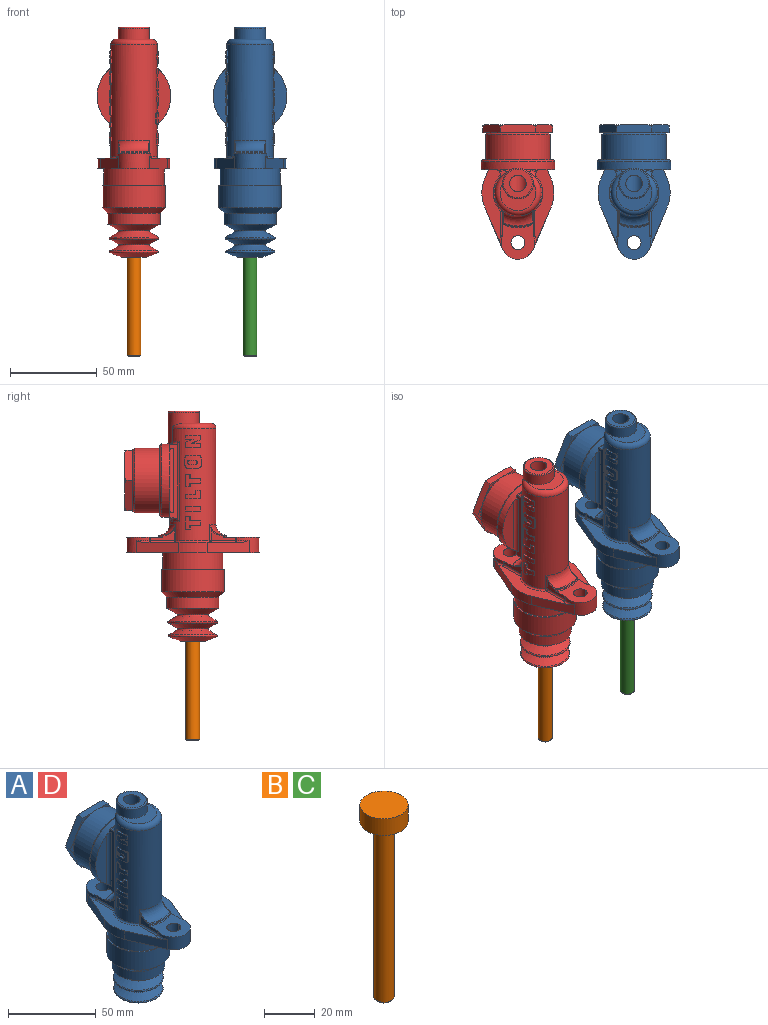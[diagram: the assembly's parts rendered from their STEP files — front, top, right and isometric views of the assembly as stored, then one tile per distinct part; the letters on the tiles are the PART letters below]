
ASSEMBLY  parts=4 mates=7
PART A: 264 faces, bbox 46.8x78.4x133.3 mm
  f0: torus R=9.44mm, axis (0,0,1), area 75.5mm2, adj f28,f29
  f1: torus R=9.44mm, axis (0,0,1), area 75.5mm2, adj f31,f32
  f2: cylinder r=14.05mm len=8.75mm, axis (0,0,1), area 34.9mm2, adj f197,f198,f199,f200,f201,f202,f203,f204
  f3: cylinder r=14.05mm len=8.75mm, axis (0,0,1), area 34.9mm2, adj f189,f190,f191,f192,f193,f194,f195,f196
  f4: cylinder r=13.3mm len=5.19mm, axis (0,0,1), area 11.7mm2, adj f181,f182,f183,f184,f185,f186,f187,f188
  f5: cylinder r=14.05mm len=9.25mm, axis (0,0,1), area 54.7mm2, adj f173,f174,f175,f176,f177,f178,f179,f180
  f6: cylinder r=14.05mm len=8.75mm, axis (0,0,1), area 52.7mm2, adj f163,f164,f165,f166,f167,f168,f169,f170
  f7: cylinder r=14.05mm len=8.75mm, axis (0,0,1), area 29.3mm2, adj f157,f158,f159,f160,f161,f162
  f8: cylinder r=14.05mm len=8.75mm, axis (0,0,1), area 23.2mm2, adj f153,f154,f155,f156
  f9: torus R=10.54mm, axis (0,0,1), area 8.4mm2, adj f15,f46,f121,f140
  f10: torus R=14.3mm, axis (0,0,1), area 35.1mm2, adj f23,f121,f136,f138
  f11: torus R=10.54mm, axis (0,0,1), area 8.4mm2, adj f16,f44,f121,f133
  f12: cylinder r=4.76mm len=37.03mm, axis (0,0,1), area 1064.2mm2, adj f13,f78
  f13: cylinder r=5.56mm len=39mm, axis (0,1,0), area 1280.3mm2, adj f12,f14,f93
  f14: cone r=5.56mm half-angle=59deg, axis (0,1,0), area 113.1mm2, adj f13
  f15: cylinder r=9.54mm len=19.09mm, axis (0,0,-1), area 230mm2, adj f9,f41,f46,f48,f69,f114,f118,f122
  f16: cylinder r=9.54mm len=19.09mm, axis (0,0,-1), area 230mm2, adj f11,f44,f47,f69,f70,f113,f119,f132
  f17: cylinder r=4mm len=9mm, axis (0,0,-1), area 226.2mm2, adj f69,f70
  f18: torus R=8.25mm, axis (0,0,1), area 55.6mm2, adj f19,f78
  f19: cylinder r=8.9mm len=18.85mm, axis (0,0,1), area 522.9mm2, adj f18,f21,f22,f23,f36,f55,f58,f76
  f20: cylinder r=9.53mm len=35.94mm, axis (0,0,1), area 2150.9mm2, adj f71,f77
  f21: torus R=10.3mm, axis (0,0,1), area 275.9mm2, adj f19,f22,f23,f76
  f22: cylinder r=13.3mm len=7.53mm, axis (0,0,1), area 46.4mm2, adj f19,f21,f23,f105,f106
  f23: cylinder r=13.3mm len=64.53mm, axis (0,0,1), area 3284.5mm2, adj f10,f19,f21,f22,f43,f75,f100,f101
  f24: cylinder r=17.3mm len=34.6mm, axis (0,0,1), area 1054.4mm2, adj f69,f73
  f25: cylinder r=18mm len=36mm, axis (0,0,1), area 1440.3mm2, adj f26,f73
  f26: cone r=18mm half-angle=45deg, axis (0,0,1), area 439.8mm2, adj f25,f27
  f27: cylinder r=15mm len=30mm, axis (0,0,1), area 602.3mm2, adj f26,f28
  f28: cone r=15mm half-angle=60deg, axis (0,0,1), area 514.8mm2, adj f0,f27
  f29: cone r=9.11mm half-angle=59deg, axis (0,0,-1), area 420.1mm2, adj f0,f30
  f30: torus R=13.72mm, axis (0,0,1), area 120.9mm2, adj f29,f31
  f31: cone r=14.04mm half-angle=60deg, axis (0,0,1), area 414.1mm2, adj f1,f30
  f32: cone r=9.11mm half-angle=59deg, axis (0,0,-1), area 397.4mm2, adj f1,f33
  f33: torus R=13.5mm, axis (0,0,1), area 128.9mm2, adj f32,f34
  f34: cone r=13.72mm half-angle=70deg, axis (0,0,1), area 458mm2, adj f33,f72
  f35: cylinder r=3.97mm len=28.5mm, axis (0,0,1), area 710.7mm2, adj f71,f72
  f36: cone r=21.11mm half-angle=0.7deg, axis (0,-1,0), area 609.8mm2, adj f19,f39,f55,f58,f59,f61,f62,f63
  f37: cone r=18.65mm half-angle=40deg, axis (0,-1,0), area 155.9mm2, adj f38,f49,f50,f51,f52,f53,f54,f81
  f38: cylinder r=18.65mm len=37.3mm, axis (0,-1,0), area 1686.5mm2, adj f37,f60
  f39: torus R=19.42mm, axis (0,-1,0), area 294.3mm2, adj f36,f60
  f40: cylinder r=20.75mm len=16.29mm, axis (0,0,-1), area 100.4mm2, adj f47,f48,f69,f116
  f41: plane 20.13x19.09mm, normal (0,0,1), area 258.8mm2, adj f15,f79,f80,f114,f115,f117,f118,f151
  f42: cylinder r=19.5mm len=17.55mm, axis (0,0,1), area 4mm2, adj f112,f120,f142,f143,f144,f152
  f43: torus R=19.54mm, axis (0,0,1), area 168.9mm2, adj f23,f141,f142,f143,f144,f145
  f44: plane 24.38x10.53mm, normal (0.92,0.39,0), area 159.4mm2, adj f11,f16,f45,f69,f121
  f45: cylinder r=20.75mm len=16.29mm, axis (0,0,-1), area 100.4mm2, adj f44,f46,f69,f121
  f46: plane 24.37x10.52mm, normal (0.92,-0.39,0), area 159.3mm2, adj f9,f15,f45,f69,f121
  f47: plane 24.4x10.54mm, normal (-0.92,0.39,0), area 159.3mm2, adj f16,f40,f69,f116,f132
  f48: plane 24.41x10.56mm, normal (-0.92,-0.39,0), area 159.3mm2, adj f15,f40,f69,f116,f122
  f49: plane 10.15x5.86mm, normal (0,-1,0), area 12mm2, adj f37,f87,f88
  f50: plane 11.72x3.38mm, normal (0,-1,0), area 12mm2, adj f37,f88,f89
  f51: plane 10.15x5.86mm, normal (0,-1,0), area 12mm2, adj f37,f89,f90
  f52: plane 10.15x5.86mm, normal (0,-1,0), area 12mm2, adj f37,f90,f91
  f53: plane 11.72x3.38mm, normal (0,-1,0), area 12mm2, adj f37,f91,f92
  f54: plane 10.15x5.86mm, normal (0,-1,0), area 12mm2, adj f37,f87,f92
  f55: plane 1.85x0.44mm, normal (0,-1,0), area 0.4mm2, adj f19,f36,f105
  f56: plane 2.74x1.99mm, normal (0,0,-1), area 2.5mm2, adj f64,f65,f109
  f57: plane 2.74x1.99mm, normal (0,0,1), area 2.5mm2, adj f63,f66,f101
  f58: plane 1.85x0.44mm, normal (0,-1,0), area 0.4mm2, adj f19,f36,f100
  f59: plane 34.46x8.87mm, normal (0,-1,0), area 214.2mm2, adj f36,f110
  f60: plane 38.84x38.84mm, normal (0,1,0), area 92mm2, adj f38,f39
  f61: plane 34.46x8.87mm, normal (0,-1,0), area 214.2mm2, adj f36,f111
  f62: plane 4.58x1.9mm, normal (0,1,0), area 3.8mm2, adj f36,f65,f68,f105
  f63: plane 4.58x1.9mm, normal (0,1,0), area 3.8mm2, adj f36,f57,f66,f100
  f64: plane 21.61x4.14mm, normal (0,1,0), area 27.2mm2, adj f36,f56,f65,f66,f67,f104,f108
  f65: plane 43.54x4.25mm, normal (1,0,0), area 103.4mm2, adj f36,f56,f62,f64,f68,f106,f107,f109
  f66: plane 43.54x4.25mm, normal (-1,0,0), area 103.4mm2, adj f36,f57,f63,f64,f67,f101,f102,f103
  f67: plane 2.74x1.99mm, normal (0,0,-1), area 2.5mm2, adj f64,f66,f103
  f68: plane 2.74x1.99mm, normal (0,0,1), area 2.5mm2, adj f62,f65,f106
  f69: plane 76.2x41.5mm, normal (0,0,-1), area 1110.8mm2, adj f15,f16,f17,f24,f40,f44,f45,f46
  f70: plane 20.13x19.09mm, normal (0,0,1), area 258.5mm2, adj f16,f17,f112,f113,f119,f120,f152
  f71: plane 19.05x19.05mm, normal (0,0,1), area 235.5mm2, adj f20,f35
  f72: plane 14.31x14.31mm, normal (0,0,-1), area 111.4mm2, adj f34,f35
  f73: plane 36x36mm, normal (0,0,1), area 77.6mm2, adj f24,f25
  f74: cylinder r=19.5mm len=17.55mm, axis (0,0,1), area 4mm2, adj f115,f117,f148,f149,f150,f151
  f75: torus R=19.54mm, axis (0,0,1), area 168.9mm2, adj f23,f146,f147,f148,f149,f150
  f76: plane 20.6x15.49mm, normal (0,0,1), area 146.4mm2, adj f19,f21
  f77: plane 19.05x19.05mm, normal (0,0,-1), area 285mm2, adj f20
  f78: plane 16.5x16.5mm, normal (0,0,1), area 142.6mm2, adj f12,f18
  f79: cylinder r=4mm len=9mm, axis (0,0,-1), area 112.8mm2, adj f41,f69,f80
  f80: cylinder r=4mm len=9mm, axis (0,0,-1), area 112.8mm2, adj f41,f69,f79
  f81: plane 5.75x3.32mm, normal (0,1,0), area 1.4mm2, adj f37,f88
  f82: plane 5.75x3.32mm, normal (0,1,0), area 1.4mm2, adj f37,f89
  f83: plane 6.64x0.31mm, normal (0,1,0), area 1.4mm2, adj f37,f90
  f84: plane 5.75x3.32mm, normal (0,1,0), area 1.4mm2, adj f37,f91
  f85: plane 5.75x3.32mm, normal (0,1,0), area 1.4mm2, adj f37,f92
  f86: plane 6.64x0.31mm, normal (0,1,0), area 1.4mm2, adj f37,f87
  f87: plane 20.34x4.67mm, normal (0,0,1), area 89.8mm2, adj f49,f54,f86,f88,f92,f93,f95,f99
  f88: plane 17.64x10.25mm, normal (-0.87,0,0.5), area 89.8mm2, adj f49,f50,f81,f87,f89,f93,f98,f99
  f89: plane 17.64x10.25mm, normal (-0.87,0,-0.5), area 89.8mm2, adj f50,f51,f82,f88,f90,f93,f97,f98
  f90: plane 20.34x4.67mm, normal (0,0,-1), area 89.8mm2, adj f51,f52,f83,f89,f91,f93,f96,f97
  f91: plane 17.64x10.25mm, normal (0.87,0,-0.5), area 89.8mm2, adj f52,f53,f84,f90,f92,f93,f94,f96
  f92: plane 17.64x10.25mm, normal (0.87,0,0.5), area 89.8mm2, adj f53,f54,f85,f87,f91,f93,f94,f95
  f93: plane 38.33x34.93mm, normal (0,1,0), area 948.4mm2, adj f13,f87,f88,f89,f90,f91,f92,f94
  f94: torus R=17.89mm, axis (0,-1,0), area 2.2mm2, adj f91,f92,f93
  f95: torus R=17.89mm, axis (0,-1,0), area 2.2mm2, adj f87,f92,f93
  f96: torus R=17.89mm, axis (0,-1,0), area 2.2mm2, adj f90,f91,f93
  f97: torus R=17.89mm, axis (0,-1,0), area 2.2mm2, adj f89,f90,f93
  f98: torus R=17.89mm, axis (0,-1,0), area 2.2mm2, adj f88,f89,f93
  f99: torus R=17.89mm, axis (0,-1,0), area 2.2mm2, adj f87,f88,f93
  f100: bspline ~4.19x2mm, area 4.9mm2, adj f19,f23,f58,f63,f101
  f101: torus R=15.3mm, axis (0,0,1), area 13.9mm2, adj f23,f57,f66,f100,f102
  f102: cylinder r=2mm len=46mm, axis (0,0,1), area 57mm2, adj f23,f66,f101,f103
  f103: torus R=15.3mm, axis (0,0,1), area 13.9mm2, adj f23,f66,f67,f102,f104
  f104: bspline ~7.56x2mm, area 7mm2, adj f23,f64,f103
  f105: bspline ~4.19x2mm, area 4.9mm2, adj f19,f22,f55,f62,f106
  f106: torus R=15.3mm, axis (0,0,1), area 13.9mm2, adj f22,f65,f68,f105,f107
  f107: cylinder r=2mm len=46mm, axis (0,0,1), area 57mm2, adj f23,f65,f106,f109
  f108: bspline ~7.56x2mm, area 7mm2, adj f23,f64,f109
  f109: torus R=15.3mm, axis (0,0,1), area 13.9mm2, adj f23,f56,f65,f107,f108
  f110: cylinder r=2mm len=37.05mm, axis (0,0,-1), area 112.3mm2, adj f36,f59,f66
  f111: cylinder r=2mm len=37.05mm, axis (0,0,-1), area 112.3mm2, adj f36,f61,f65
  f112: plane 14.07x6.94mm, normal (-1,0,0), area 41.6mm2, adj f42,f70,f113,f127,f130,f144,f152
  f113: cylinder r=2mm len=2mm, axis (0,0,-1), area 1.5mm2, adj f16,f70,f112,f131
  f114: cylinder r=2mm len=2mm, axis (0,0,-1), area 1.5mm2, adj f15,f41,f115,f123
  f115: plane 14.07x6.94mm, normal (-1,0,0), area 41.6mm2, adj f41,f74,f114,f124,f125,f148,f151
  f116: plane 56.36x10.98mm, normal (0,0,1), area 302.9mm2, adj f40,f47,f48,f122,f123,f125,f128,f130
  f117: plane 14.07x6.94mm, normal (1,0,0), area 41.6mm2, adj f41,f74,f118,f137,f139,f149,f151
  f118: cylinder r=2mm len=2mm, axis (0,0,-1), area 1.5mm2, adj f15,f41,f117,f140
  f119: cylinder r=2mm len=2mm, axis (0,0,-1), area 1.5mm2, adj f16,f70,f120,f133
  f120: plane 14.07x6.94mm, normal (1,0,0), area 41.6mm2, adj f42,f70,f119,f134,f135,f142,f152
  f121: plane 56.36x10.98mm, normal (0,0,1), area 302.9mm2, adj f9,f10,f11,f44,f45,f46,f133,f135
  f122: torus R=10.54mm, axis (0,0,1), area 8.5mm2, adj f15,f48,f116,f123
  f123: torus R=1mm, axis (0,0,1), area 0.9mm2, adj f114,f116,f122,f125
  f124: cylinder r=1mm len=9.44mm, axis (0,0,1), area 6.7mm2, adj f23,f115,f126,f146
  f125: cylinder r=1mm len=13.97mm, axis (0,-1,0), area 21.9mm2, adj f115,f116,f123,f126
  f126: sphere r=1mm, area 0.6mm2, adj f124,f125,f128
  f127: cylinder r=1mm len=9.44mm, axis (0,0,1), area 6.7mm2, adj f23,f112,f129,f145
  f128: torus R=14.3mm, axis (0,0,1), area 35.1mm2, adj f23,f116,f126,f129
  f129: sphere r=1mm, area 0.6mm2, adj f127,f128,f130
  f130: cylinder r=1mm len=13.97mm, axis (0,-1,0), area 21.9mm2, adj f112,f116,f129,f131
  f131: torus R=1mm, axis (0,0,1), area 0.9mm2, adj f113,f116,f130,f132
  f132: torus R=10.54mm, axis (0,0,1), area 8.5mm2, adj f16,f47,f116,f131
  f133: torus R=1mm, axis (0,0,1), area 0.9mm2, adj f11,f119,f121,f135
  f134: cylinder r=1mm len=9.44mm, axis (0,0,1), area 6.7mm2, adj f23,f120,f136,f141
  f135: cylinder r=1mm len=13.97mm, axis (0,1,0), area 21.9mm2, adj f120,f121,f133,f136
  f136: sphere r=1mm, area 0.6mm2, adj f10,f134,f135
  f137: cylinder r=1mm len=9.44mm, axis (0,0,1), area 6.7mm2, adj f23,f117,f138,f147
  f138: sphere r=1mm, area 0.6mm2, adj f10,f137,f139
  f139: cylinder r=1mm len=13.97mm, axis (0,1,0), area 21.9mm2, adj f117,f121,f138,f140
  f140: torus R=1mm, axis (0,0,1), area 0.9mm2, adj f9,f118,f121,f139
  f141: bspline ~2.6x1.1mm, area 0.4mm2, adj f43,f134,f142
  f142: bspline ~7.04x4.34mm, area 5.1mm2, adj f42,f43,f120,f141,f143
  f143: torus R=19mm, axis (0,0,-1), area 13.2mm2, adj f42,f43,f142,f144
  f144: bspline ~7.04x4.34mm, area 5.1mm2, adj f42,f43,f112,f143,f145
  f145: bspline ~2.6x1.09mm, area 0.4mm2, adj f43,f127,f144
  f146: bspline ~2.6x1.09mm, area 0.4mm2, adj f75,f124,f148
  f147: bspline ~2.6x1.09mm, area 0.4mm2, adj f75,f137,f149
  f148: bspline ~7.04x4.34mm, area 5.1mm2, adj f74,f75,f115,f146,f150
  f149: bspline ~7.04x4.34mm, area 5.1mm2, adj f74,f75,f117,f147,f150
  f150: torus R=19mm, axis (0,0,-1), area 13.2mm2, adj f74,f75,f148,f149
  f151: torus R=20mm, axis (0,0,1), area 14.2mm2, adj f41,f74,f115,f117
  f152: torus R=20mm, axis (0,0,1), area 14.2mm2, adj f42,f70,f112,f120
  f153: plane 2.61x0.71mm, normal (-0.33,-0.94,0), area 2mm2, adj f8,f23,f154,f156
  f154: plane 8.75x1.49mm, normal (0,0,-1), area 6.5mm2, adj f8,f23,f153,f155
  f155: plane 2.61x0.72mm, normal (-0.29,0.96,0), area 2mm2, adj f8,f23,f154,f156
  f156: plane 8.75x1.49mm, normal (0,0,1), area 6.5mm2, adj f8,f23,f153,f155
  f157: plane 5x0.71mm, normal (-0.33,-0.94,0), area 3.7mm2, adj f7,f23,f158,f162
  f158: plane 2.85x1.37mm, normal (0,0,-1), area 2.1mm2, adj f7,f23,f157,f159
  f159: plane 2.5x0.74mm, normal (0.13,0.99,0), area 1.9mm2, adj f7,f23,f158,f160
  f160: plane 6x1.33mm, normal (0,0,-1), area 4.4mm2, adj f7,f23,f159,f161
  f161: plane 2.5x0.72mm, normal (-0.29,0.96,0), area 1.9mm2, adj f7,f23,f160,f162
  f162: plane 8.75x1.49mm, normal (0,0,1), area 6.5mm2, adj f7,f23,f157,f161
  f163: plane 2.36x0.71mm, normal (-0.33,-0.94,0), area 1.8mm2, adj f6,f23,f164,f172
  f164: plane 5.22x1.49mm, normal (0,0,-1), area 3.9mm2, adj f6,f23,f163,f165
  f165: bspline ~5.22x1.85mm, area 4.1mm2, adj f6,f23,f164,f166
  f166: plane 2.69x0.71mm, normal (-0.33,-0.94,0), area 2mm2, adj f6,f23,f165,f167
  f167: plane 8.75x1.49mm, normal (0,0,-1), area 6.5mm2, adj f6,f23,f166,f168
  f168: plane 2.26x0.72mm, normal (-0.29,0.96,0), area 1.7mm2, adj f6,f23,f167,f169
  f169: plane 4.44x1.33mm, normal (0,0,1), area 3.3mm2, adj f6,f23,f168,f170
  f170: bspline ~4.45x1.71mm, area 3.5mm2, adj f6,f23,f169,f171
  f171: plane 2.93x0.72mm, normal (-0.29,0.96,0), area 2.2mm2, adj f6,f23,f170,f172
  f172: plane 8.75x1.49mm, normal (0,0,1), area 6.5mm2, adj f6,f23,f163,f171
  f173: bspline ~1.69x1.5mm, area 1.8mm2, adj f5,f23,f174,f180
  f174: plane 6.21x1.14mm, normal (0,0,-1), area 4.6mm2, adj f5,f23,f173,f175
  f175: bspline ~1.68x1.5mm, area 1.8mm2, adj f5,f23,f174,f176
  f176: plane 4.33x0.71mm, normal (-0.31,0.95,0), area 3.2mm2, adj f5,f23,f175,f177
  f177: bspline ~1.68x1.5mm, area 1.8mm2, adj f5,f23,f176,f178
  f178: plane 6.21x1.14mm, normal (0,0,1), area 4.6mm2, adj f5,f23,f177,f179
  f179: bspline ~1.69x1.5mm, area 1.8mm2, adj f5,f23,f178,f180
  f180: plane 4.33x0.7mm, normal (-0.35,-0.94,0), area 3.2mm2, adj f5,f23,f173,f179
  f181: bspline ~1.14x1mm, area 1.2mm2, adj f4,f5,f182,f188
  f182: plane 0.73x0.41mm, normal (0.2,-0.98,0), area 0.3mm2, adj f4,f5,f181,f183
  f183: bspline ~1.14x1mm, area 1.2mm2, adj f4,f5,f182,f184
  f184: plane 3.4x0.86mm, normal (0,0,-1), area 2.5mm2, adj f4,f5,f183,f185
  f185: bspline ~1.13x1mm, area 1.2mm2, adj f4,f5,f184,f186
  f186: plane 0.74x0.41mm, normal (0.19,0.98,0), area 0.3mm2, adj f4,f5,f185,f187
  f187: bspline ~1.13x1mm, area 1.2mm2, adj f4,f5,f186,f188
  f188: plane 3.4x0.86mm, normal (0,0,1), area 2.5mm2, adj f4,f5,f181,f187
  f189: plane 2.61x0.71mm, normal (-0.33,-0.94,0), area 2mm2, adj f3,f23,f190,f196
  f190: plane 6.13x1.49mm, normal (0,0,-1), area 4.5mm2, adj f3,f23,f189,f191
  f191: plane 2.32x0.75mm, normal (0.11,-0.99,0), area 1.7mm2, adj f3,f23,f190,f192
  f192: plane 2.7x1.25mm, normal (0,0,-1), area 2mm2, adj f3,f23,f191,f193
  f193: plane 7x0.72mm, normal (-0.29,0.96,0), area 5.2mm2, adj f3,f23,f192,f194
  f194: plane 2.7x1.25mm, normal (0,0,1), area 2mm2, adj f3,f23,f193,f195
  f195: plane 2.07x0.75mm, normal (0.11,-0.99,0), area 1.6mm2, adj f3,f23,f194,f196
  f196: plane 6.13x1.49mm, normal (0,0,1), area 4.5mm2, adj f3,f23,f189,f195
  f197: plane 2.61x0.71mm, normal (-0.33,-0.94,0), area 2mm2, adj f2,f23,f198,f204
  f198: plane 6.13x1.49mm, normal (0,0,-1), area 4.5mm2, adj f2,f23,f197,f199
  f199: plane 2.32x0.75mm, normal (0.11,-0.99,0), area 1.7mm2, adj f2,f23,f198,f200
  f200: plane 2.7x1.25mm, normal (0,0,-1), area 2mm2, adj f2,f23,f199,f201
  f201: plane 7x0.72mm, normal (-0.29,0.96,0), area 5.2mm2, adj f2,f23,f200,f202
  f202: plane 2.7x1.25mm, normal (0,0,1), area 2mm2, adj f2,f23,f201,f203
  f203: plane 2.07x0.75mm, normal (0.11,-0.99,0), area 1.6mm2, adj f2,f23,f202,f204
  f204: plane 6.13x1.49mm, normal (0,0,1), area 4.5mm2, adj f2,f23,f197,f203
  f205: bspline ~1.69x1.5mm, area 1.8mm2, adj f23,f206,f212,f213
  f206: plane 4.33x0.71mm, normal (0.34,-0.94,0), area 3.2mm2, adj f23,f205,f207,f213
  f207: bspline ~1.69x1.5mm, area 1.8mm2, adj f23,f206,f208,f213
  f208: plane 6.21x1.1mm, normal (0,0,-1), area 4.6mm2, adj f23,f207,f209,f213
  f209: bspline ~1.69x1.5mm, area 1.8mm2, adj f23,f208,f210,f213
  f210: plane 4.33x0.71mm, normal (0.32,0.95,0), area 3.2mm2, adj f23,f209,f211,f213
  f211: bspline ~1.69x1.5mm, area 1.8mm2, adj f23,f210,f212,f213
  f212: plane 6.21x1.1mm, normal (0,0,1), area 4.6mm2, adj f23,f205,f211,f213
  f213: cylinder r=14.05mm len=9.25mm, axis (0,0,1), area 54.7mm2, adj f205,f206,f207,f208,f209,f210,f211,f212
  f214: bspline ~1.15x1mm, area 1.2mm2, adj f213,f215,f221,f222
  f215: plane 3.4x0.88mm, normal (0,0,-1), area 2.5mm2, adj f213,f214,f216,f222
  f216: bspline ~1.12x1mm, area 1.2mm2, adj f213,f215,f217,f222
  f217: plane 0.74x0.41mm, normal (-0.17,0.98,0), area 0.3mm2, adj f213,f216,f218,f222
  f218: bspline ~1.12x1mm, area 1.2mm2, adj f213,f217,f219,f222
  f219: plane 3.4x0.88mm, normal (0,0,1), area 2.5mm2, adj f213,f218,f220,f222
  f220: bspline ~1.15x1mm, area 1.2mm2, adj f213,f219,f221,f222
  f221: plane 0.73x0.41mm, normal (-0.22,-0.98,0), area 0.3mm2, adj f213,f214,f220,f222
  f222: cylinder r=13.3mm len=5.19mm, axis (0,0,1), area 11.7mm2, adj f214,f215,f216,f217,f218,f219,f220,f221
  f223: plane 6.14x1.44mm, normal (0,0,1), area 4.5mm2, adj f23,f224,f230,f231
  f224: plane 2.32x0.74mm, normal (-0.12,-0.99,0), area 1.7mm2, adj f23,f223,f225,f231
  f225: plane 2.7x1.28mm, normal (0,0,1), area 2mm2, adj f23,f224,f226,f231
  f226: plane 7x0.71mm, normal (0.3,0.95,0), area 5.2mm2, adj f23,f225,f227,f231
  f227: plane 2.7x1.28mm, normal (0,0,-1), area 2mm2, adj f23,f226,f228,f231
  f228: plane 2.07x0.74mm, normal (-0.12,-0.99,0), area 1.6mm2, adj f23,f227,f229,f231
  f229: plane 6.14x1.44mm, normal (0,0,-1), area 4.5mm2, adj f23,f228,f230,f231
  f230: plane 2.61x0.71mm, normal (0.32,-0.95,0), area 2mm2, adj f23,f223,f229,f231
  f231: cylinder r=14.05mm len=8.75mm, axis (0,0,1), area 34.9mm2, adj f223,f224,f225,f226,f227,f228,f229,f230
  f232: plane 6.14x1.44mm, normal (0,0,-1), area 4.5mm2, adj f23,f233,f239,f240
  f233: plane 2.61x0.71mm, normal (0.32,-0.95,0), area 2mm2, adj f23,f232,f234,f240
  f234: plane 6.14x1.44mm, normal (0,0,1), area 4.5mm2, adj f23,f233,f235,f240
  f235: plane 2.32x0.74mm, normal (-0.12,-0.99,0), area 1.7mm2, adj f23,f234,f236,f240
  f236: plane 2.7x1.28mm, normal (0,0,1), area 2mm2, adj f23,f235,f237,f240
  f237: plane 7x0.71mm, normal (0.3,0.95,0), area 5.2mm2, adj f23,f236,f238,f240
  f238: plane 2.7x1.28mm, normal (0,0,-1), area 2mm2, adj f23,f237,f239,f240
  f239: plane 2.07x0.74mm, normal (-0.12,-0.99,0), area 1.6mm2, adj f23,f232,f238,f240
  f240: cylinder r=14.05mm len=8.75mm, axis (0,0,1), area 34.9mm2, adj f232,f233,f234,f235,f236,f237,f238,f239
  f241: plane 2.5x0.71mm, normal (0.3,0.95,0), area 1.9mm2, adj f23,f242,f246,f247
  f242: plane 6x1.38mm, normal (0,0,1), area 4.4mm2, adj f23,f241,f243,f247
  f243: plane 2.5x0.74mm, normal (-0.12,0.99,0), area 1.9mm2, adj f23,f242,f244,f247
  f244: plane 2.85x1.34mm, normal (0,0,1), area 2.1mm2, adj f23,f243,f245,f247
  f245: plane 5x0.71mm, normal (0.32,-0.95,0), area 3.7mm2, adj f23,f244,f246,f247
  f246: plane 8.75x1.44mm, normal (0,0,-1), area 6.5mm2, adj f23,f241,f245,f247
  f247: cylinder r=14.05mm len=8.75mm, axis (0,0,1), area 29.3mm2, adj f241,f242,f243,f244,f245,f246
  f248: plane 4.44x1.38mm, normal (0,0,-1), area 3.3mm2, adj f23,f249,f257,f258
  f249: plane 2.26x0.71mm, normal (0.3,0.95,0), area 1.7mm2, adj f23,f248,f250,f258
  f250: plane 8.75x1.44mm, normal (0,0,1), area 6.5mm2, adj f23,f249,f251,f258
  f251: plane 2.69x0.71mm, normal (0.32,-0.95,0), area 2mm2, adj f23,f250,f252,f258
  f252: bspline ~5.23x1.85mm, area 4.1mm2, adj f23,f251,f253,f258
  f253: plane 5.23x1.44mm, normal (0,0,1), area 3.9mm2, adj f23,f252,f254,f258
  f254: plane 2.36x0.71mm, normal (0.32,-0.95,0), area 1.8mm2, adj f23,f253,f255,f258
  f255: plane 8.75x1.44mm, normal (0,0,-1), area 6.5mm2, adj f23,f254,f256,f258
  f256: plane 2.93x0.71mm, normal (0.3,0.95,0), area 2.2mm2, adj f23,f255,f257,f258
  f257: bspline ~4.44x1.71mm, area 3.5mm2, adj f23,f248,f256,f258
  f258: cylinder r=14.05mm len=8.75mm, axis (0,0,1), area 52.7mm2, adj f248,f249,f250,f251,f252,f253,f254,f255
  f259: plane 8.75x1.44mm, normal (0,0,-1), area 6.5mm2, adj f23,f260,f262,f263
  f260: plane 2.61x0.71mm, normal (0.3,0.95,0), area 2mm2, adj f23,f259,f261,f263
  f261: plane 8.75x1.44mm, normal (0,0,1), area 6.5mm2, adj f23,f260,f262,f263
  f262: plane 2.61x0.71mm, normal (0.32,-0.95,0), area 2mm2, adj f23,f259,f261,f263
  f263: cylinder r=14.05mm len=8.75mm, axis (0,0,1), area 23.2mm2, adj f259,f260,f261,f262
PART B: 6 faces, bbox 19.1x19.1x93.7 mm
  f0: cone r=3.97mm half-angle=45deg, axis (0,0,1), area 30.8mm2, adj f1,f3
  f1: cylinder r=3.97mm len=84.65mm, axis (0,0,-1), area 2110.9mm2, adj f0,f5
  f2: cylinder r=9.53mm len=19.05mm, axis (0,0,-1), area 478.8mm2, adj f4,f5
  f3: plane 5.94x5.94mm, normal (0,0,-1), area 27.7mm2, adj f0
  f4: plane 19.05x19.05mm, normal (0,0,1), area 285mm2, adj f2
  f5: plane 19.05x19.05mm, normal (0,0,-1), area 235.5mm2, adj f1,f2
PART C: same geometry as B
PART D: same geometry as A
PLACE A t=(4,28.58,-13.21)mm
PLACE B t=(-62.8,28.58,-61.38)mm
PLACE C t=(4,28.58,-61.38)mm
PLACE D t=(-62.8,28.58,-13.21)mm
MATE planar D.f0 <-> B.f1  axis (0,0,-1) through (-62.8,28.57,0)mm
MATE fastened A.f13 <-> D.f93  axis (0,1,0) through (4.01,67.66,41.65)mm
MATE slider C.f1 <-> A.f0  axis (0,0,-1) through (4,28.58,-64.88)mm
MATE planar A.f36 <-> D.f36  axis (0,1,0) through (4,67.66,41.66)mm
MATE planar A.f69 <-> C.f1  axis (0,0,-1) through (-9.93,48.8,0)mm
MATE slider B.f1 <-> D.f0  axis (0,0,-1) through (-62.8,28.58,-64.88)mm
MATE planar A.f0 <-> D.f0  axis (0,0,-1) through (4,28.57,0)mm
